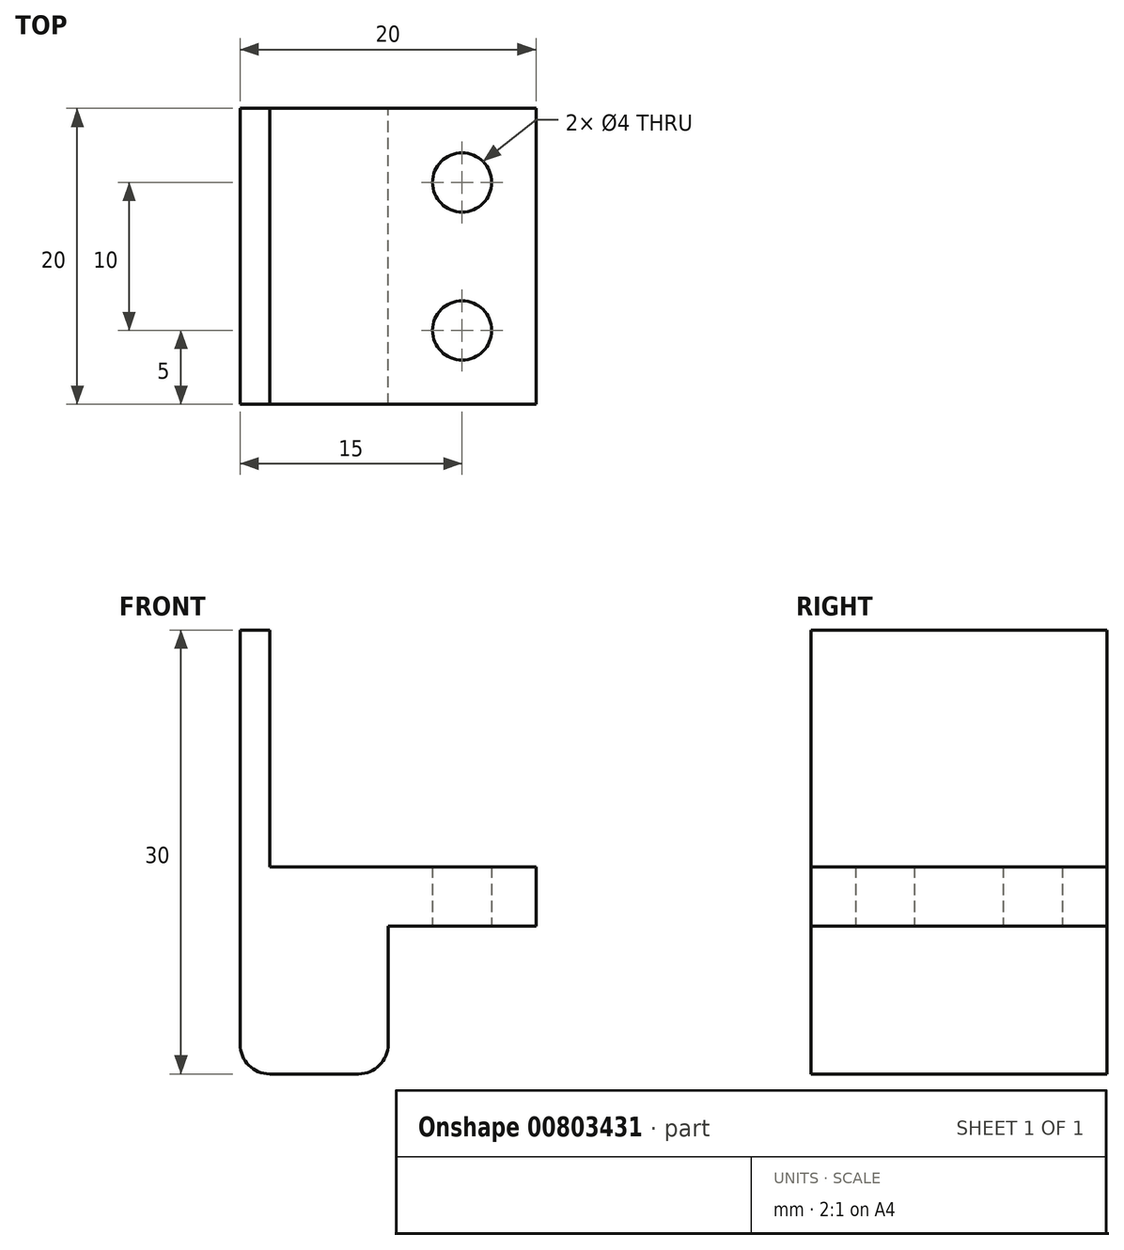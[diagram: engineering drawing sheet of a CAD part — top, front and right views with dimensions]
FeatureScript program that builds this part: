
annotation { "Feature Type Name" : "Feature", "Feature Type Description" : "" }
export const myFeature = defineFeature(function(context is Context, id is Id, definition is map)
    precondition{}
    {
        {
            var Q0;
            Q0=qCreatedBy(makeId("Front.planeOp"),FACE);
            var sketch = newSketch(context, id + "F0", { "sketchPlane" : qUnion([Q0])});
            skLineSegment(sketch, "E0", {"start": v(0, 0) * mm, "end": v(0, 16) * mm});
            skLineSegment(sketch, "E1", {"start": v(0, 16) * mm, "end": v(-2, 16) * mm});
            skLineSegment(sketch, "E2", {"start": v(0, 0) * mm, "end": v(18, 0) * mm});
            skLineSegment(sketch, "E3", {"start": v(-2, 16) * mm, "end": v(-2, -14) * mm});
            skLineSegment(sketch, "E4", {"start": v(-2, -14) * mm, "end": v(8, -14) * mm});
            skLineSegment(sketch, "E5", {"start": v(8, -14) * mm, "end": v(8, -4) * mm});
            skLineSegment(sketch, "E6", {"start": v(8, -4) * mm, "end": v(18, -4) * mm});
            skLineSegment(sketch, "E7", {"start": v(18, -4) * mm, "end": v(18, 0) * mm});
            skSolve(sketch);
        }
        {
            var Q0;
            Q0=makeQuery(id+"F0.imprint","IMPRINT",FACE,{"disambiguationData":[TD([[makeQuery(id+"F0.imprint","IMPRINT",EDGE,{"derivedFrom":sQuery(id+"F0.wireOp",EDGE,"E0")}),1.0]])]});
            extrude(context, id + "F1", {"entities" : qUnion([Q0]), "depth" : 20 * mm, "offsetDistance" : 25 * mm});
        }
        {
            var Q0;
            Q0=makeQuery(id+"F1.opExtrude","SWEPT_FACE",FACE,{"disambiguationData":[OSD([sQuery(id+"F0.wireOp",EDGE,"E6")])]});
            var sketch = newSketch(context, id + "F2", { "sketchPlane" : qUnion([Q0])});
            skPoint(sketch, "E8", {"position": v(13, 15) * mm});
            skPoint(sketch, "E9", {"position": v(13, 5) * mm});
            skCircle(sketch, "E10", {"center": v(13, 15) * mm, "radius": 2 * mm});
            skCircle(sketch, "E11", {"center": v(13, 5) * mm, "radius": 2 * mm});
            skSolve(sketch);
        }
        {
            var Q0;
            Q0=makeQuery(id+"F2.imprint","IMPRINT",FACE,{"disambiguationData":[TD([[makeQuery(id+"F2.imprint","IMPRINT",EDGE,{"derivedFrom":sQuery(id+"F2.wireOp",EDGE,"E10")}),1.0]])]});
            var Q1;
            Q1=makeQuery(id+"F2.imprint","IMPRINT",FACE,{"disambiguationData":[TD([[makeQuery(id+"F2.imprint","IMPRINT",EDGE,{"derivedFrom":sQuery(id+"F2.wireOp",EDGE,"E11")}),1.0]])]});
            extrude(context, id + "F3", {"entities" : qUnion([Q0, Q1]), "operationType" : NewBodyOperationType.REMOVE, "oppositeDirection" : true, "depth" : 25 * mm, "offsetDistance" : 25 * mm});
        }
        {
            var Q0;
            Q0=makeQuery(id+"F1.opExtrude","SWEPT_EDGE",EDGE,{"disambiguationData":[OSD([sQuery(id+"F0.wireOp",EDGE,"E3"),sQuery(id+"F0.wireOp",EDGE,"E4")])]});
            fillet(context, id + "F4", {"entities" : qUnion([Q0]), "radius" : 2 * mm, "tangentPropagation" : true, "allowEdgeOverflow" : false});
        }
        {
            var Q0;
            Q0=makeQuery(id+"F1.opExtrude","SWEPT_EDGE",EDGE,{"disambiguationData":[OSD([sQuery(id+"F0.wireOp",EDGE,"E4"),sQuery(id+"F0.wireOp",EDGE,"E5")])]});
            fillet(context, id + "F5", {"entities" : qUnion([Q0]), "radius" : 2 * mm, "tangentPropagation" : true, "allowEdgeOverflow" : false});
        }
    });
